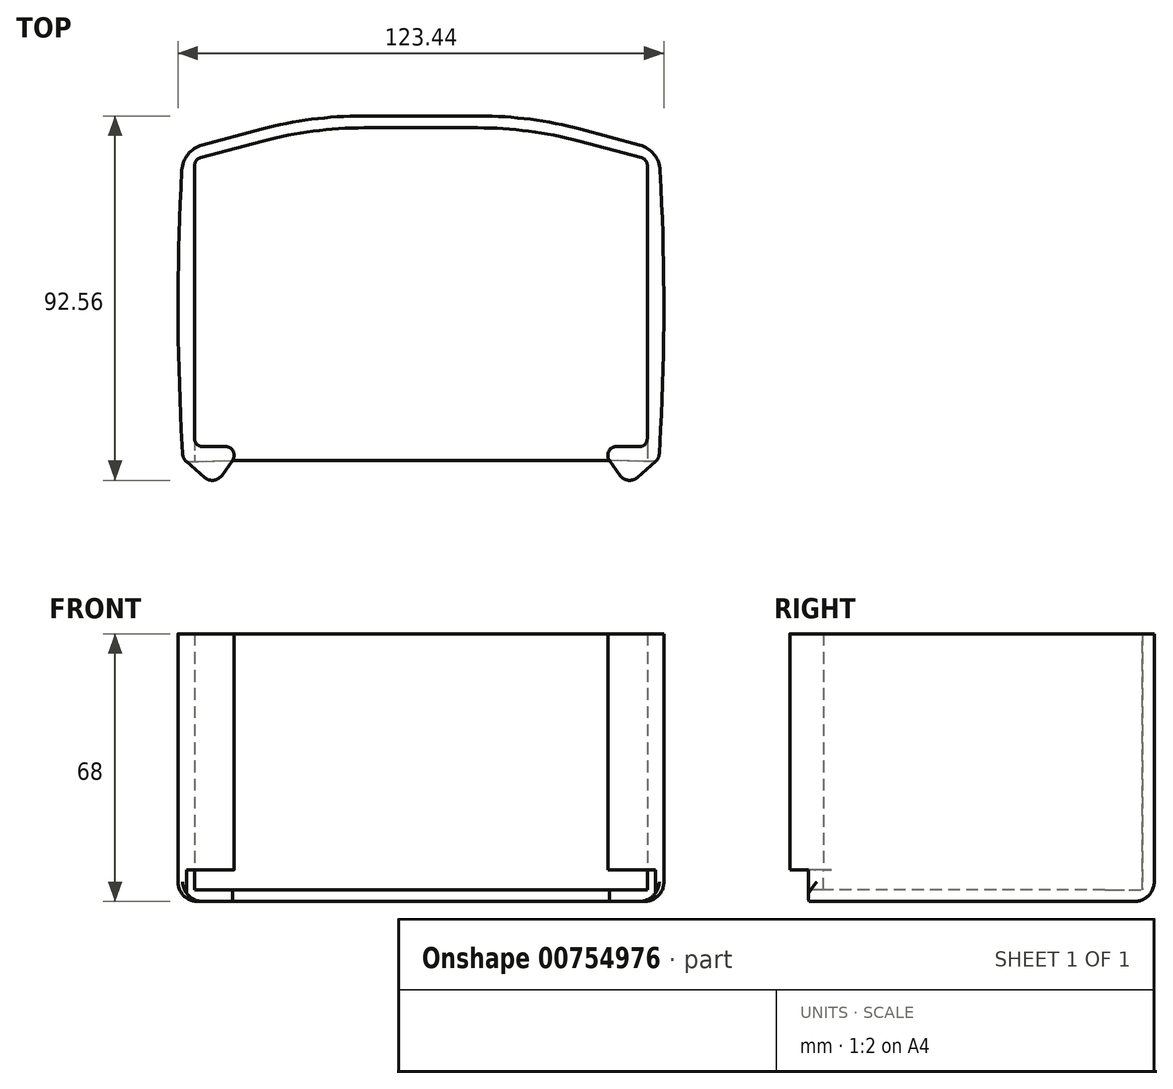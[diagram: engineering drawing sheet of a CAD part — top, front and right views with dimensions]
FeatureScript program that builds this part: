
annotation { "Feature Type Name" : "Feature", "Feature Type Description" : "" }
export const myFeature = defineFeature(function(context is Context, id is Id, definition is map)
    precondition{}
    {
        {
            var Q0;
            Q0=qCreatedBy(makeId("Top.planeOp"),FACE);
            var sketch = newSketch(context, id + "F0", { "sketchPlane" : qUnion([Q0])});
            skLineSegment(sketch, "E0", {"start": v(105.89, 0) * mm, "end": v(105.89, -73) * mm});
            skLineSegment(sketch, "E1", {"start": v(-9.11, 0) * mm, "end": v(-9.11, -73) * mm});
            skLineSegment(sketch, "E2", {"start": v(-9.11, -73) * mm, "end": v(0.89, -73) * mm});
            skLineSegment(sketch, "E3", {"start": v(0.89, -73) * mm, "end": v(0.89, -76) * mm});
            skLineSegment(sketch, "E4", {"start": v(95.89, -76) * mm, "end": v(95.89, -73) * mm});
            skLineSegment(sketch, "E5", {"start": v(95.89, -73) * mm, "end": v(105.89, -73) * mm});
            skLineSegment(sketch, "E6", {"start": v(-12.11, 2.3) * mm, "end": v(20.5, 11) * mm});
            skLineSegment(sketch, "E7", {"start": v(76.28, 11) * mm, "end": v(108.89, 2.3) * mm});
            skLineSegment(sketch, "E8", {"start": v(-9.11, 0) * mm, "end": v(20.89, 8) * mm});
            skLineSegment(sketch, "E9", {"start": v(20.89, 8) * mm, "end": v(75.89, 8) * mm});
            skLineSegment(sketch, "E10", {"start": v(75.89, 8) * mm, "end": v(105.89, 0) * mm});
            skLineSegment(sketch, "E11", {"start": v(20.5, 11) * mm, "end": v(76.28, 11) * mm});
            skLineSegment(sketch, "E12", {"start": v(108.89, 2.3) * mm, "end": v(110.89, -38) * mm});
            skLineSegment(sketch, "E13", {"start": v(110.89, -38) * mm, "end": v(108.89, -76) * mm});
            skLineSegment(sketch, "E14", {"start": v(-12.11, 2.3) * mm, "end": v(-14.11, -38) * mm});
            skLineSegment(sketch, "E15", {"start": v(-14.11, -38) * mm, "end": v(-12.11, -76) * mm});
            skLineSegment(sketch, "E16", {"start": v(108.89, -76) * mm, "end": v(100.89, -83) * mm});
            skLineSegment(sketch, "E17", {"start": v(100.89, -83) * mm, "end": v(95.89, -76) * mm});
            skLineSegment(sketch, "E18", {"start": v(-12.11, -76) * mm, "end": v(-4.11, -83) * mm});
            skLineSegment(sketch, "E19", {"start": v(-4.11, -83) * mm, "end": v(0.89, -76) * mm});
            skSolve(sketch);
        }
        {
            var Q0;
            Q0 = qSketchRegion(id + "F0", true);
            extrude(context, id + "F1", {"entities" : qUnion([Q0]), "depth" : 60 * mm, "offsetDistance" : 25 * mm});
        }
        {
            var Q0;
            Q0=makeQuery(id+"F1.opExtrude","SWEPT_EDGE",EDGE,{"disambiguationData":[OSD([sQuery(id+"F0.wireOp",EDGE,"Ie72LNE6-8cUq-577t-HtWn-rKg7aSPlHmMY"),sQuery(id+"F0.wireOp",EDGE,"mTkdWyBM-IY4b-tw5D-a9xK-fEVKUx1Kd3wm")])]});
            var Q1;
            Q1=makeQuery(id+"F1.opExtrude","SWEPT_EDGE",EDGE,{"disambiguationData":[OSD([sQuery(id+"F0.wireOp",EDGE,"WxkxMuoK-TSDW-V2qn-Z2qn-Agb6PySI1a7b"),sQuery(id+"F0.wireOp",EDGE,"Ie72LNE6-8cUq-577t-HtWn-rKg7aSPlHmMY")])]});
            var Q2;
            Q2=makeQuery(id+"F1.opExtrude","SWEPT_EDGE",EDGE,{"disambiguationData":[OSD([sQuery(id+"F0.wireOp",EDGE,"YWlqvh6o-r7vO-u0KY-qpqE-FjMp1Y8u6ouf"),sQuery(id+"F0.wireOp",EDGE,"mrutAYqv-b8EF-A8OW-RZmt-WUMPHs9cScPi")])]});
            var Q3;
            Q3=makeQuery(id+"F1.opExtrude","SWEPT_EDGE",EDGE,{"disambiguationData":[OSD([sQuery(id+"F0.wireOp",EDGE,"mrutAYqv-b8EF-A8OW-RZmt-WUMPHs9cScPi"),sQuery(id+"F0.wireOp",EDGE,"WxkxMuoK-TSDW-V2qn-Z2qn-Agb6PySI1a7b")])]});
            var Q4;
            Q4=makeQuery(id+"F1.opExtrude","SWEPT_EDGE",EDGE,{"disambiguationData":[OSD([sQuery(id+"F0.wireOp",EDGE,"E3"),sQuery(id+"F0.wireOp",EDGE,"YWlqvh6o-r7vO-u0KY-qpqE-FjMp1Y8u6ouf")])]});
            var Q5;
            Q5=makeQuery(id+"F1.opExtrude","SWEPT_EDGE",EDGE,{"disambiguationData":[OSD([sQuery(id+"F0.wireOp",EDGE,"mTkdWyBM-IY4b-tw5D-a9xK-fEVKUx1Kd3wm"),sQuery(id+"F0.wireOp",EDGE,"E4")])]});
            fillet(context, id + "F2", {"entities" : qUnion([Q0, Q1, Q2, Q3, Q4, Q5]), "radius" : 2 * mm, "tangentPropagation" : true, "allowEdgeOverflow" : false});
        }
        {
            var Q0;
            Q0=makeQuery(id+"F1.opExtrude","SWEPT_EDGE",EDGE,{"disambiguationData":[OSD([sQuery(id+"F0.wireOp",EDGE,"tW5Z51e3-Nlht-Tmme-xamD-BKYe6IWbI0Vi"),sQuery(id+"F0.wireOp",EDGE,"E1")])]});
            var Q1;
            Q1=makeQuery(id+"F1.opExtrude","SWEPT_EDGE",EDGE,{"disambiguationData":[OSD([sQuery(id+"F0.wireOp",EDGE,"tW5Z51e3-Nlht-Tmme-xamD-BKYe6IWbI0Vi"),sQuery(id+"F0.wireOp",EDGE,"E0")])]});
            fillet(context, id + "F3", {"entities" : qUnion([Q0, Q1]), "radius" : 2 * mm, "tangentPropagation" : true, "allowEdgeOverflow" : false});
        }
        {
            var Q0;
            Q0=makeQuery(id+"F1.opExtrude","SWEPT_EDGE",EDGE,{"disambiguationData":[OSD([sQuery(id+"F0.wireOp",EDGE,"E7"),sQuery(id+"F0.wireOp",EDGE,"E11")])]});
            var Q1;
            Q1=makeQuery(id+"F1.opExtrude","SWEPT_EDGE",EDGE,{"disambiguationData":[OSD([sQuery(id+"F0.wireOp",EDGE,"E6"),sQuery(id+"F0.wireOp",EDGE,"E11")])]});
            var Q2;
            Q2=makeQuery(id+"F1.opExtrude","SWEPT_EDGE",EDGE,{"disambiguationData":[OSD([sQuery(id+"F0.wireOp",EDGE,"E8"),sQuery(id+"F0.wireOp",EDGE,"E9")])]});
            var Q3;
            Q3=makeQuery(id+"F1.opExtrude","SWEPT_EDGE",EDGE,{"disambiguationData":[OSD([sQuery(id+"F0.wireOp",EDGE,"E9"),sQuery(id+"F0.wireOp",EDGE,"E10")])]});
            fillet(context, id + "F4", {"entities" : qUnion([Q0, Q1, Q2, Q3]), "radius" : 100 * mm, "tangentPropagation" : true, "rho" : 0.5, "crossSection" : FilletCrossSection.CONIC, "allowEdgeOverflow" : false});
        }
        {
            var Q0;
            Q0=makeQuery(id+"F1.opExtrude","SWEPT_EDGE",EDGE,{"disambiguationData":[OSD([sQuery(id+"F0.wireOp",EDGE,"E12"),sQuery(id+"F0.wireOp",EDGE,"E13")])]});
            var Q1;
            Q1=makeQuery(id+"F1.opExtrude","SWEPT_EDGE",EDGE,{"disambiguationData":[OSD([sQuery(id+"F0.wireOp",EDGE,"E14"),sQuery(id+"F0.wireOp",EDGE,"E15")])]});
            fillet(context, id + "F5", {"entities" : qUnion([Q0, Q1]), "radius" : 600 * mm, "tangentPropagation" : true, "allowEdgeOverflow" : false});
        }
        {
            var Q0;
            Q0=makeQuery(id+"F1.opExtrude","SWEPT_EDGE",EDGE,{"disambiguationData":[OSD([sQuery(id+"F0.wireOp",EDGE,"E7"),sQuery(id+"F0.wireOp",EDGE,"E12")])]});
            var Q1;
            Q1=makeQuery(id+"F1.opExtrude","SWEPT_EDGE",EDGE,{"disambiguationData":[OSD([sQuery(id+"F0.wireOp",EDGE,"E6"),sQuery(id+"F0.wireOp",EDGE,"E14")])]});
            fillet(context, id + "F6", {"entities" : qUnion([Q0, Q1]), "radius" : 7 * mm, "tangentPropagation" : true, "allowEdgeOverflow" : false});
        }
        {
            var Q0;
            Q0=makeQuery(id+"F1.opExtrude","SWEPT_EDGE",EDGE,{"disambiguationData":[OSD([sQuery(id+"F0.wireOp",EDGE,"E13"),sQuery(id+"F0.wireOp",EDGE,"E16")])]});
            var Q1;
            Q1=makeQuery(id+"F1.opExtrude","SWEPT_EDGE",EDGE,{"disambiguationData":[OSD([sQuery(id+"F0.wireOp",EDGE,"E15"),sQuery(id+"F0.wireOp",EDGE,"E18")])]});
            var Q2;
            Q2=makeQuery(id+"F1.opExtrude","SWEPT_EDGE",EDGE,{"disambiguationData":[OSD([sQuery(id+"F0.wireOp",EDGE,"E18"),sQuery(id+"F0.wireOp",EDGE,"E19")])]});
            var Q3;
            Q3=makeQuery(id+"F1.opExtrude","SWEPT_EDGE",EDGE,{"disambiguationData":[OSD([sQuery(id+"F0.wireOp",EDGE,"E16"),sQuery(id+"F0.wireOp",EDGE,"E17")])]});
            fillet(context, id + "F7", {"entities" : qUnion([Q0, Q1, Q2, Q3]), "radius" : 3 * mm, "tangentPropagation" : true, "allowEdgeOverflow" : false});
        }
        {
            var Q0;
            Q0=makeQuery(id+"F1.opExtrude","CAP_FACE",FACE,{"disambiguationData":[OSD([sQuery(id+"F0.wireOp",EDGE,"E0"),sQuery(id+"F0.wireOp",EDGE,"E1"),sQuery(id+"F0.wireOp",EDGE,"E2"),sQuery(id+"F0.wireOp",EDGE,"E3"),sQuery(id+"F0.wireOp",EDGE,"E4"),sQuery(id+"F0.wireOp",EDGE,"E5"),sQuery(id+"F0.wireOp",EDGE,"E6"),sQuery(id+"F0.wireOp",EDGE,"E7"),sQuery(id+"F0.wireOp",EDGE,"E8"),sQuery(id+"F0.wireOp",EDGE,"E9"),sQuery(id+"F0.wireOp",EDGE,"E10"),sQuery(id+"F0.wireOp",EDGE,"E11"),sQuery(id+"F0.wireOp",EDGE,"E12"),sQuery(id+"F0.wireOp",EDGE,"E13"),sQuery(id+"F0.wireOp",EDGE,"E14"),sQuery(id+"F0.wireOp",EDGE,"E15"),sQuery(id+"F0.wireOp",EDGE,"E16"),sQuery(id+"F0.wireOp",EDGE,"E17"),sQuery(id+"F0.wireOp",EDGE,"E18"),sQuery(id+"F0.wireOp",EDGE,"E19")])],"isStart":true});
            var sketch = newSketch(context, id + "F8", { "sketchPlane" : qUnion([Q0])});
            skArc(sketch, "E20.0.1", {"start": v(-11.16, 76.83) * mm, "mid": v(-11.88, 75.89) * mm, "end": v(-12.18, 74.73) * mm});
            skLineSegment(sketch, "E20.0.2", {"start": v(-12.18, 74.73) * mm, "end": v(-12.5, 68.63) * mm});
            skArc(sketch, "E20.0.3", {"start": v(-12.5, 68.63) * mm, "mid": v(-13.33, 38) * mm, "end": v(-12.6, 7.36) * mm});
            skLineSegment(sketch, "E20.0.4", {"start": v(-12.6, 7.36) * mm, "end": v(-12.37, 2.8) * mm});
            skArc(sketch, "E20.0.5", {"start": v(-12.37, 2.8) * mm, "mid": v(-10.82, -1.26) * mm, "end": v(-7.18, -3.62) * mm});
            skLineSegment(sketch, "E20.0.6", {"start": v(-7.18, -3.62) * mm, "end": v(7.83, -7.62) * mm});
            skFitSpline(sketch, "E20.0.7", {"points": [v(7.83, -7.62) * mm, v(16.27, -9.87) * mm, v(24.86, -11) * mm, v(33.6, -11) * mm]});
            skLineSegment(sketch, "E20.0.8", {"start": v(33.6, -11) * mm, "end": v(63.18, -11) * mm});
            skFitSpline(sketch, "E20.0.9", {"points": [v(63.18, -11) * mm, v(71.91, -11) * mm, v(80.5, -9.87) * mm, v(88.94, -7.62) * mm]});
            skLineSegment(sketch, "E20.0.10", {"start": v(88.94, -7.62) * mm, "end": v(103.95, -3.62) * mm});
            skArc(sketch, "E20.0.11", {"start": v(103.95, -3.62) * mm, "mid": v(107.6, -1.26) * mm, "end": v(109.14, 2.8) * mm});
            skLineSegment(sketch, "E20.0.12", {"start": v(109.14, 2.8) * mm, "end": v(109.37, 7.36) * mm});
            skArc(sketch, "E20.0.13", {"start": v(109.37, 7.36) * mm, "mid": v(110.1, 38) * mm, "end": v(109.28, 68.63) * mm});
            skLineSegment(sketch, "E20.0.14", {"start": v(109.28, 68.63) * mm, "end": v(108.95, 74.73) * mm});
            skArc(sketch, "E20.0.15", {"start": v(108.95, 74.73) * mm, "mid": v(108.66, 75.89) * mm, "end": v(107.93, 76.83) * mm});
            skLineSegment(sketch, "E20.0.20", {"start": v(95.89, 75.36) * mm, "end": v(95.89, 75) * mm});
            skLineSegment(sketch, "E20.0.36", {"start": v(0.89, 75) * mm, "end": v(0.89, 75.36) * mm});
            skArc(sketch, "E20.0.37", {"start": v(0.89, 75.36) * mm, "mid": v(0.8, 75.97) * mm, "end": v(0.52, 76.52) * mm});
            skLineSegment(sketch, "E21", {"start": v(107.93, 76.83) * mm, "end": v(96.26, 76.52) * mm});
            skLineSegment(sketch, "E22", {"start": v(-11.16, 76.83) * mm, "end": v(0.52, 76.52) * mm});
            skLineSegment(sketch, "E23", {"start": v(96.26, 76.52) * mm, "end": v(0.52, 76.52) * mm});
            skLineSegment(sketch, "E24", {"start": v(-9.11, 10) * mm, "end": v(105.89, 10) * mm});
            skLineSegment(sketch, "E25", {"start": v(105.89, 10) * mm, "end": v(105.89, 73) * mm});
            skLineSegment(sketch, "E26", {"start": v(105.89, 73) * mm, "end": v(-9.11, 73) * mm});
            skLineSegment(sketch, "E27", {"start": v(-9.11, 73) * mm, "end": v(-9.11, 10) * mm});
            skLineSegment(sketch, "E28", {"start": v(105.89, 10) * mm, "end": v(109.5, 10) * mm});
            skLineSegment(sketch, "E29", {"start": v(-9.11, 10) * mm, "end": v(-12.72, 10) * mm});
            skLineSegment(sketch, "E30", {"start": v(-9.11, 73) * mm, "end": v(-9.11, 76.78) * mm});
            skLineSegment(sketch, "E31", {"start": v(105.89, 73) * mm, "end": v(105.96, 76.78) * mm});
            skLineSegment(sketch, "E32", {"start": v(105.89, 5.13) * mm, "end": v(109.26, 5.13) * mm});
            skLineSegment(sketch, "E33", {"start": v(105.89, 5.13) * mm, "end": v(-9.11, 5.13) * mm});
            skLineSegment(sketch, "E34", {"start": v(-9.11, 5.13) * mm, "end": v(-12.48, 5.13) * mm});
            skSolve(sketch);
        }
        {
            var Q0;
            {var subQ8=sQuery(id+"F8.wireOp",EDGE,"E20.0.14");Q0=makeQuery(id+"F8.imprint","IMPRINT",FACE,{"disambiguationData":[TD([[makeQuery(id+"F8.imprint","IMPRINT",EDGE,{"derivedFrom":subQ8}),1.0]])]});}
            var Q1;
            {var subQ1=sQuery(id+"F8.wireOp",EDGE,"E28");Q1=makeQuery(id+"F8.imprint","IMPRINT",FACE,{"disambiguationData":[TD([[makeQuery(id+"F8.imprint","IMPRINT",EDGE,{"derivedFrom":subQ1}),-1.0]])]});}
            var Q2;
            {var subQ4=sQuery(id+"F8.wireOp",EDGE,"E20.0.5");Q2=makeQuery(id+"F8.imprint","IMPRINT",FACE,{"disambiguationData":[TD([[makeQuery(id+"F8.imprint","IMPRINT",EDGE,{"derivedFrom":subQ4}),1.0]])]});}
            var Q3;
            {var subQ1=sQuery(id+"F8.wireOp",EDGE,"E29");Q3=makeQuery(id+"F8.imprint","IMPRINT",FACE,{"disambiguationData":[TD([[makeQuery(id+"F8.imprint","IMPRINT",EDGE,{"derivedFrom":subQ1}),1.0]])]});}
            var Q4;
            {var subQ1=sQuery(id+"F8.wireOp",EDGE,"E20.0.1");Q4=makeQuery(id+"F8.imprint","IMPRINT",FACE,{"disambiguationData":[TD([[makeQuery(id+"F8.imprint","IMPRINT",EDGE,{"derivedFrom":subQ1}),1.0]])]});}
            extrude(context, id + "F9", {"entities" : qUnion([Q0, Q1, Q2, Q3, Q4]), "operationType" : NewBodyOperationType.ADD, "depth" : (3 + 5) * mm, "offsetDistance" : 25 * mm});
        }
        {
            var Q0;
            {var subQ13=sQuery(id+"F8.wireOp",EDGE,"E24");Q0=makeQuery(id+"F8.imprint","IMPRINT",FACE,{"disambiguationData":[TD([[makeQuery(id+"F8.imprint","IMPRINT",EDGE,{"derivedFrom":subQ13}),1.0]])]});}
            var Q1;
            {var subQ1=sQuery(id+"F0.wireOp",EDGE,"E5");var subQ2=sQuery(id+"F0.wireOp",EDGE,"E0");var subQ3=makeQuery(id+"F3.opFillet","BLEND_EDGE",EDGE,{"blendedFrom":[makeQuery(id+"F1.opExtrude","SWEPT_EDGE",EDGE,{"disambiguationData":[OSD([subQ2,subQ1])]}),makeQuery(id+"F1.opExtrude","CAP_FACE",FACE,{"disambiguationData":[OSD([subQ2,sQuery(id+"F0.wireOp",EDGE,"E1"),sQuery(id+"F0.wireOp",EDGE,"E2"),sQuery(id+"F0.wireOp",EDGE,"E3"),sQuery(id+"F0.wireOp",EDGE,"E4"),subQ1,sQuery(id+"F0.wireOp",EDGE,"E6"),sQuery(id+"F0.wireOp",EDGE,"E7"),sQuery(id+"F0.wireOp",EDGE,"E8"),sQuery(id+"F0.wireOp",EDGE,"E9"),sQuery(id+"F0.wireOp",EDGE,"E10"),sQuery(id+"F0.wireOp",EDGE,"E11"),sQuery(id+"F0.wireOp",EDGE,"E12"),sQuery(id+"F0.wireOp",EDGE,"E13"),sQuery(id+"F0.wireOp",EDGE,"E14"),sQuery(id+"F0.wireOp",EDGE,"E15"),sQuery(id+"F0.wireOp",EDGE,"E16"),sQuery(id+"F0.wireOp",EDGE,"E17"),sQuery(id+"F0.wireOp",EDGE,"E18"),sQuery(id+"F0.wireOp",EDGE,"E19")])],"isStart":true})],"blendedInto":[makeQuery(id+"F1.opExtrude","CAP_FACE",FACE,{"disambiguationData":[OSD([subQ2,sQuery(id+"F0.wireOp",EDGE,"E1"),sQuery(id+"F0.wireOp",EDGE,"E2"),sQuery(id+"F0.wireOp",EDGE,"E3"),sQuery(id+"F0.wireOp",EDGE,"E4"),subQ1,sQuery(id+"F0.wireOp",EDGE,"E6"),sQuery(id+"F0.wireOp",EDGE,"E7"),sQuery(id+"F0.wireOp",EDGE,"E8"),sQuery(id+"F0.wireOp",EDGE,"E9"),sQuery(id+"F0.wireOp",EDGE,"E10"),sQuery(id+"F0.wireOp",EDGE,"E11"),sQuery(id+"F0.wireOp",EDGE,"E12"),sQuery(id+"F0.wireOp",EDGE,"E13"),sQuery(id+"F0.wireOp",EDGE,"E14"),sQuery(id+"F0.wireOp",EDGE,"E15"),sQuery(id+"F0.wireOp",EDGE,"E16"),sQuery(id+"F0.wireOp",EDGE,"E17"),sQuery(id+"F0.wireOp",EDGE,"E18"),sQuery(id+"F0.wireOp",EDGE,"E19")])],"isStart":true})]});Q1=makeQuery(id+"F8.imprint","IMPRINT",FACE,{"disambiguationData":[TD([[makeQuery(id+"F8.imprint","IMPRINT",EDGE,{"derivedFrom":subQ3}),1.0]])]});}
            var Q2;
            Q2=makeQuery(id+"F8.imprint","IMPRINT",FACE,{"disambiguationData":[TD([[makeQuery(id+"F8.imprint","IMPRINT",EDGE,{"derivedFrom":sQuery(id+"F8.wireOp",EDGE,"E20.0.20")}),1.0]])]});
            var Q3;
            Q3=makeQuery(id+"F8.imprint","IMPRINT",FACE,{"disambiguationData":[TD([[makeQuery(id+"F8.imprint","IMPRINT",EDGE,{"derivedFrom":sQuery(id+"F8.wireOp",EDGE,"E20.0.20")}),-1.0]])]});
            var Q4;
            Q4=makeQuery(id+"F8.imprint","IMPRINT",FACE,{"disambiguationData":[TD([[makeQuery(id+"F8.imprint","IMPRINT",EDGE,{"derivedFrom":sQuery(id+"F8.wireOp",EDGE,"E20.0.36")}),1.0]])]});
            var Q5;
            {var subQ1=sQuery(id+"F0.wireOp",EDGE,"E2");var subQ2=sQuery(id+"F0.wireOp",EDGE,"E1");var subQ3=makeQuery(id+"F3.opFillet","BLEND_EDGE",EDGE,{"blendedFrom":[makeQuery(id+"F1.opExtrude","SWEPT_EDGE",EDGE,{"disambiguationData":[OSD([subQ2,subQ1])]}),makeQuery(id+"F1.opExtrude","CAP_FACE",FACE,{"disambiguationData":[OSD([sQuery(id+"F0.wireOp",EDGE,"E0"),subQ2,subQ1,sQuery(id+"F0.wireOp",EDGE,"E3"),sQuery(id+"F0.wireOp",EDGE,"E4"),sQuery(id+"F0.wireOp",EDGE,"E5"),sQuery(id+"F0.wireOp",EDGE,"E6"),sQuery(id+"F0.wireOp",EDGE,"E7"),sQuery(id+"F0.wireOp",EDGE,"E8"),sQuery(id+"F0.wireOp",EDGE,"E9"),sQuery(id+"F0.wireOp",EDGE,"E10"),sQuery(id+"F0.wireOp",EDGE,"E11"),sQuery(id+"F0.wireOp",EDGE,"E12"),sQuery(id+"F0.wireOp",EDGE,"E13"),sQuery(id+"F0.wireOp",EDGE,"E14"),sQuery(id+"F0.wireOp",EDGE,"E15"),sQuery(id+"F0.wireOp",EDGE,"E16"),sQuery(id+"F0.wireOp",EDGE,"E17"),sQuery(id+"F0.wireOp",EDGE,"E18"),sQuery(id+"F0.wireOp",EDGE,"E19")])],"isStart":true})],"blendedInto":[makeQuery(id+"F1.opExtrude","CAP_FACE",FACE,{"disambiguationData":[OSD([sQuery(id+"F0.wireOp",EDGE,"E0"),subQ2,subQ1,sQuery(id+"F0.wireOp",EDGE,"E3"),sQuery(id+"F0.wireOp",EDGE,"E4"),sQuery(id+"F0.wireOp",EDGE,"E5"),sQuery(id+"F0.wireOp",EDGE,"E6"),sQuery(id+"F0.wireOp",EDGE,"E7"),sQuery(id+"F0.wireOp",EDGE,"E8"),sQuery(id+"F0.wireOp",EDGE,"E9"),sQuery(id+"F0.wireOp",EDGE,"E10"),sQuery(id+"F0.wireOp",EDGE,"E11"),sQuery(id+"F0.wireOp",EDGE,"E12"),sQuery(id+"F0.wireOp",EDGE,"E13"),sQuery(id+"F0.wireOp",EDGE,"E14"),sQuery(id+"F0.wireOp",EDGE,"E15"),sQuery(id+"F0.wireOp",EDGE,"E16"),sQuery(id+"F0.wireOp",EDGE,"E17"),sQuery(id+"F0.wireOp",EDGE,"E18"),sQuery(id+"F0.wireOp",EDGE,"E19")])],"isStart":true})]});Q5=makeQuery(id+"F8.imprint","IMPRINT",FACE,{"disambiguationData":[TD([[makeQuery(id+"F8.imprint","IMPRINT",EDGE,{"derivedFrom":subQ3}),1.0]])]});}
            var Q6;
            {var subQ0=sQuery(id+"F8.wireOp",EDGE,"E24");Q6=makeQuery(id+"F8.imprint","IMPRINT",FACE,{"disambiguationData":[TD([[makeQuery(id+"F8.imprint","IMPRINT",EDGE,{"derivedFrom":subQ0}),-1.0]])]});}
            var Q7;
            {var subQ9=sQuery(id+"F8.wireOp",EDGE,"E33");Q7=makeQuery(id+"F8.imprint","IMPRINT",FACE,{"disambiguationData":[TD([[makeQuery(id+"F8.imprint","IMPRINT",EDGE,{"derivedFrom":subQ9}),1.0]])]});}
            extrude(context, id + "F10", {"entities" : qUnion([Q0, Q1, Q2, Q3, Q4, Q5, Q6, Q7]), "operationType" : NewBodyOperationType.ADD, "depth" : (3 + 5) * mm, "offsetDistance" : 25 * mm, "hasSecondDirection" : true, "secondDirectionOppositeDirection" : true, "secondDirectionDepth" : -5 * mm});
        }
        {
            var Q0;
            Q0=makeQuery(id+"F9.opExtrude","CAP_EDGE",EDGE,{"disambiguationData":[OSD([sQuery(id+"F8.wireOp",EDGE,"E20.0.8")])],"isStart":false});
            fillet(context, id + "F11", {"entities" : qUnion([Q0]), "radius" : 5 * mm, "tangentPropagation" : true, "allowEdgeOverflow" : false});
        }
    });
